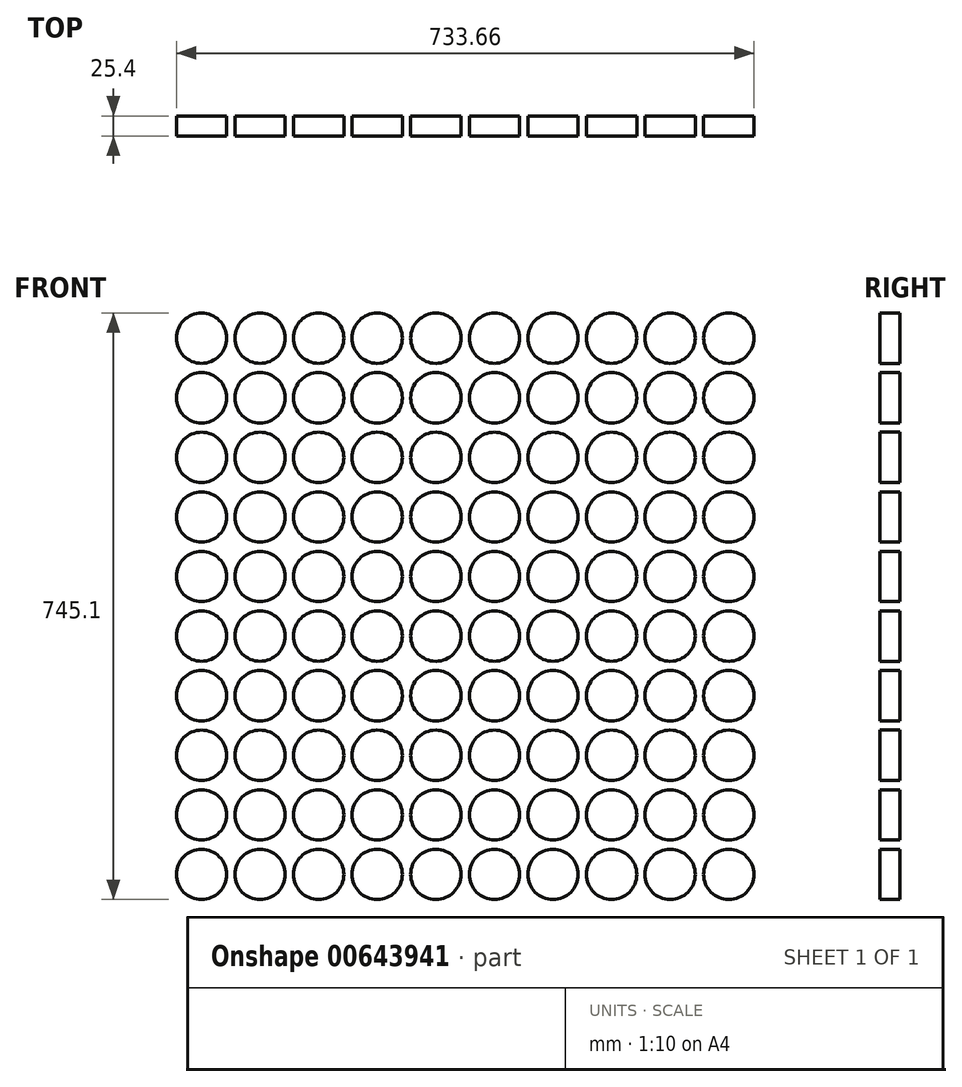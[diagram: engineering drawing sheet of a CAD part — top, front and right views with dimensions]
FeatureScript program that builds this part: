
annotation { "Feature Type Name" : "Feature", "Feature Type Description" : "" }
export const myFeature = defineFeature(function(context is Context, id is Id, definition is map)
    precondition{}
    {
        {
            var Q0;
            Q0=qCreatedBy(makeId("Front.planeOp"),FACE);
            var sketch = newSketch(context, id + "F0", { "sketchPlane" : qUnion([Q0])});
            skCircle(sketch, "E0", {"center": v(-124.64, -78.12) * mm, "radius": 31.93 * mm});
            skCircle(sketch, "E1.0.1.0", {"center": v(-124.64, -2.43) * mm, "radius": 31.93 * mm});
            skCircle(sketch, "E1.0.2.0", {"center": v(-124.64, 73.26) * mm, "radius": 31.93 * mm});
            skCircle(sketch, "E1.0.3.0", {"center": v(-124.64, 148.95) * mm, "radius": 31.93 * mm});
            skCircle(sketch, "E1.0.4.0", {"center": v(-124.64, 224.64) * mm, "radius": 31.93 * mm});
            skCircle(sketch, "E1.0.5.0", {"center": v(-124.64, 300.34) * mm, "radius": 31.93 * mm});
            skCircle(sketch, "E1.0.6.0", {"center": v(-124.64, 376.03) * mm, "radius": 31.93 * mm});
            skCircle(sketch, "E1.0.7.0", {"center": v(-124.64, 451.72) * mm, "radius": 31.93 * mm});
            skCircle(sketch, "E1.0.8.0", {"center": v(-124.64, 527.41) * mm, "radius": 31.93 * mm});
            skCircle(sketch, "E1.0.9.0", {"center": v(-124.64, 603.1) * mm, "radius": 31.93 * mm});
            skCircle(sketch, "E1.1.0.0", {"center": v(-50.22, -78.12) * mm, "radius": 31.93 * mm});
            skCircle(sketch, "E1.1.1.0", {"center": v(-50.22, -2.43) * mm, "radius": 31.93 * mm});
            skCircle(sketch, "E1.1.2.0", {"center": v(-50.22, 73.26) * mm, "radius": 31.93 * mm});
            skCircle(sketch, "E1.1.3.0", {"center": v(-50.22, 148.95) * mm, "radius": 31.93 * mm});
            skCircle(sketch, "E1.1.4.0", {"center": v(-50.22, 224.64) * mm, "radius": 31.93 * mm});
            skCircle(sketch, "E1.1.5.0", {"center": v(-50.22, 300.34) * mm, "radius": 31.93 * mm});
            skCircle(sketch, "E1.1.6.0", {"center": v(-50.22, 376.03) * mm, "radius": 31.93 * mm});
            skCircle(sketch, "E1.1.7.0", {"center": v(-50.22, 451.72) * mm, "radius": 31.93 * mm});
            skCircle(sketch, "E1.1.8.0", {"center": v(-50.22, 527.41) * mm, "radius": 31.93 * mm});
            skCircle(sketch, "E1.1.9.0", {"center": v(-50.22, 603.1) * mm, "radius": 31.93 * mm});
            skCircle(sketch, "E1.2.0.0", {"center": v(24.2, -78.12) * mm, "radius": 31.93 * mm});
            skCircle(sketch, "E1.2.1.0", {"center": v(24.2, -2.43) * mm, "radius": 31.93 * mm});
            skCircle(sketch, "E1.2.2.0", {"center": v(24.2, 73.26) * mm, "radius": 31.93 * mm});
            skCircle(sketch, "E1.2.3.0", {"center": v(24.2, 148.95) * mm, "radius": 31.93 * mm});
            skCircle(sketch, "E1.2.4.0", {"center": v(24.2, 224.64) * mm, "radius": 31.93 * mm});
            skCircle(sketch, "E1.2.5.0", {"center": v(24.2, 300.34) * mm, "radius": 31.93 * mm});
            skCircle(sketch, "E1.2.6.0", {"center": v(24.2, 376.03) * mm, "radius": 31.93 * mm});
            skCircle(sketch, "E1.2.7.0", {"center": v(24.2, 451.72) * mm, "radius": 31.93 * mm});
            skCircle(sketch, "E1.2.8.0", {"center": v(24.2, 527.41) * mm, "radius": 31.93 * mm});
            skCircle(sketch, "E1.2.9.0", {"center": v(24.2, 603.1) * mm, "radius": 31.93 * mm});
            skCircle(sketch, "E1.3.0.0", {"center": v(98.63, -78.12) * mm, "radius": 31.93 * mm});
            skCircle(sketch, "E1.3.1.0", {"center": v(98.63, -2.43) * mm, "radius": 31.93 * mm});
            skCircle(sketch, "E1.3.2.0", {"center": v(98.63, 73.26) * mm, "radius": 31.93 * mm});
            skCircle(sketch, "E1.3.3.0", {"center": v(98.63, 148.95) * mm, "radius": 31.93 * mm});
            skCircle(sketch, "E1.3.4.0", {"center": v(98.63, 224.64) * mm, "radius": 31.93 * mm});
            skCircle(sketch, "E1.3.5.0", {"center": v(98.63, 300.34) * mm, "radius": 31.93 * mm});
            skCircle(sketch, "E1.3.6.0", {"center": v(98.63, 376.03) * mm, "radius": 31.93 * mm});
            skCircle(sketch, "E1.3.7.0", {"center": v(98.63, 451.72) * mm, "radius": 31.93 * mm});
            skCircle(sketch, "E1.3.8.0", {"center": v(98.63, 527.41) * mm, "radius": 31.93 * mm});
            skCircle(sketch, "E1.3.9.0", {"center": v(98.63, 603.1) * mm, "radius": 31.93 * mm});
            skCircle(sketch, "E1.4.0.0", {"center": v(173.05, -78.12) * mm, "radius": 31.93 * mm});
            skCircle(sketch, "E1.4.1.0", {"center": v(173.05, -2.43) * mm, "radius": 31.93 * mm});
            skCircle(sketch, "E1.4.2.0", {"center": v(173.05, 73.26) * mm, "radius": 31.93 * mm});
            skCircle(sketch, "E1.4.3.0", {"center": v(173.05, 148.95) * mm, "radius": 31.93 * mm});
            skCircle(sketch, "E1.4.4.0", {"center": v(173.05, 224.64) * mm, "radius": 31.93 * mm});
            skCircle(sketch, "E1.4.5.0", {"center": v(173.05, 300.34) * mm, "radius": 31.93 * mm});
            skCircle(sketch, "E1.4.6.0", {"center": v(173.05, 376.03) * mm, "radius": 31.93 * mm});
            skCircle(sketch, "E1.4.7.0", {"center": v(173.05, 451.72) * mm, "radius": 31.93 * mm});
            skCircle(sketch, "E1.4.8.0", {"center": v(173.05, 527.41) * mm, "radius": 31.93 * mm});
            skCircle(sketch, "E1.4.9.0", {"center": v(173.05, 603.1) * mm, "radius": 31.93 * mm});
            skCircle(sketch, "E1.5.0.0", {"center": v(247.47, -78.12) * mm, "radius": 31.93 * mm});
            skCircle(sketch, "E1.5.1.0", {"center": v(247.47, -2.43) * mm, "radius": 31.93 * mm});
            skCircle(sketch, "E1.5.2.0", {"center": v(247.47, 73.26) * mm, "radius": 31.93 * mm});
            skCircle(sketch, "E1.5.3.0", {"center": v(247.47, 148.95) * mm, "radius": 31.93 * mm});
            skCircle(sketch, "E1.5.4.0", {"center": v(247.47, 224.64) * mm, "radius": 31.93 * mm});
            skCircle(sketch, "E1.5.5.0", {"center": v(247.47, 300.34) * mm, "radius": 31.93 * mm});
            skCircle(sketch, "E1.5.6.0", {"center": v(247.47, 376.03) * mm, "radius": 31.93 * mm});
            skCircle(sketch, "E1.5.7.0", {"center": v(247.47, 451.72) * mm, "radius": 31.93 * mm});
            skCircle(sketch, "E1.5.8.0", {"center": v(247.47, 527.41) * mm, "radius": 31.93 * mm});
            skCircle(sketch, "E1.5.9.0", {"center": v(247.47, 603.1) * mm, "radius": 31.93 * mm});
            skCircle(sketch, "E1.6.0.0", {"center": v(321.9, -78.12) * mm, "radius": 31.93 * mm});
            skCircle(sketch, "E1.6.1.0", {"center": v(321.9, -2.43) * mm, "radius": 31.93 * mm});
            skCircle(sketch, "E1.6.2.0", {"center": v(321.9, 73.26) * mm, "radius": 31.93 * mm});
            skCircle(sketch, "E1.6.3.0", {"center": v(321.9, 148.95) * mm, "radius": 31.93 * mm});
            skCircle(sketch, "E1.6.4.0", {"center": v(321.9, 224.64) * mm, "radius": 31.93 * mm});
            skCircle(sketch, "E1.6.5.0", {"center": v(321.9, 300.34) * mm, "radius": 31.93 * mm});
            skCircle(sketch, "E1.6.6.0", {"center": v(321.9, 376.03) * mm, "radius": 31.93 * mm});
            skCircle(sketch, "E1.6.7.0", {"center": v(321.9, 451.72) * mm, "radius": 31.93 * mm});
            skCircle(sketch, "E1.6.8.0", {"center": v(321.9, 527.41) * mm, "radius": 31.93 * mm});
            skCircle(sketch, "E1.6.9.0", {"center": v(321.9, 603.1) * mm, "radius": 31.93 * mm});
            skCircle(sketch, "E1.7.0.0", {"center": v(396.31, -78.12) * mm, "radius": 31.93 * mm});
            skCircle(sketch, "E1.7.1.0", {"center": v(396.31, -2.43) * mm, "radius": 31.93 * mm});
            skCircle(sketch, "E1.7.2.0", {"center": v(396.31, 73.26) * mm, "radius": 31.93 * mm});
            skCircle(sketch, "E1.7.3.0", {"center": v(396.31, 148.95) * mm, "radius": 31.93 * mm});
            skCircle(sketch, "E1.7.4.0", {"center": v(396.31, 224.64) * mm, "radius": 31.93 * mm});
            skCircle(sketch, "E1.7.5.0", {"center": v(396.31, 300.34) * mm, "radius": 31.93 * mm});
            skCircle(sketch, "E1.7.6.0", {"center": v(396.31, 376.03) * mm, "radius": 31.93 * mm});
            skCircle(sketch, "E1.7.7.0", {"center": v(396.31, 451.72) * mm, "radius": 31.93 * mm});
            skCircle(sketch, "E1.7.8.0", {"center": v(396.31, 527.41) * mm, "radius": 31.93 * mm});
            skCircle(sketch, "E1.7.9.0", {"center": v(396.31, 603.1) * mm, "radius": 31.93 * mm});
            skCircle(sketch, "E1.8.0.0", {"center": v(470.74, -78.12) * mm, "radius": 31.93 * mm});
            skCircle(sketch, "E1.8.1.0", {"center": v(470.74, -2.43) * mm, "radius": 31.93 * mm});
            skCircle(sketch, "E1.8.2.0", {"center": v(470.74, 73.26) * mm, "radius": 31.93 * mm});
            skCircle(sketch, "E1.8.3.0", {"center": v(470.74, 148.95) * mm, "radius": 31.93 * mm});
            skCircle(sketch, "E1.8.4.0", {"center": v(470.74, 224.64) * mm, "radius": 31.93 * mm});
            skCircle(sketch, "E1.8.5.0", {"center": v(470.74, 300.34) * mm, "radius": 31.93 * mm});
            skCircle(sketch, "E1.8.6.0", {"center": v(470.74, 376.03) * mm, "radius": 31.93 * mm});
            skCircle(sketch, "E1.8.7.0", {"center": v(470.74, 451.72) * mm, "radius": 31.93 * mm});
            skCircle(sketch, "E1.8.8.0", {"center": v(470.74, 527.41) * mm, "radius": 31.93 * mm});
            skCircle(sketch, "E1.8.9.0", {"center": v(470.74, 603.1) * mm, "radius": 31.93 * mm});
            skCircle(sketch, "E1.9.0.0", {"center": v(545.16, -78.12) * mm, "radius": 31.93 * mm});
            skCircle(sketch, "E1.9.1.0", {"center": v(545.16, -2.43) * mm, "radius": 31.93 * mm});
            skCircle(sketch, "E1.9.2.0", {"center": v(545.16, 73.26) * mm, "radius": 31.93 * mm});
            skCircle(sketch, "E1.9.3.0", {"center": v(545.16, 148.95) * mm, "radius": 31.93 * mm});
            skCircle(sketch, "E1.9.4.0", {"center": v(545.16, 224.64) * mm, "radius": 31.93 * mm});
            skCircle(sketch, "E1.9.5.0", {"center": v(545.16, 300.34) * mm, "radius": 31.93 * mm});
            skCircle(sketch, "E1.9.6.0", {"center": v(545.16, 376.03) * mm, "radius": 31.93 * mm});
            skCircle(sketch, "E1.9.7.0", {"center": v(545.16, 451.72) * mm, "radius": 31.93 * mm});
            skCircle(sketch, "E1.9.8.0", {"center": v(545.16, 527.41) * mm, "radius": 31.93 * mm});
            skCircle(sketch, "E1.9.9.0", {"center": v(545.16, 603.1) * mm, "radius": 31.93 * mm});
            skLineSegment(sketch, "E1.direction1", {"start": v(-124.64, -78.12) * mm, "end": v(-50.22, -78.12) * mm, "construction": true});
            skLineSegment(sketch, "E1.direction2", {"start": v(-124.64, -78.12) * mm, "end": v(-124.64, -2.43) * mm, "construction": true});
            skSolve(sketch);
        }
        {
            var Q0;
            Q0 = qSketchRegion(id + "F0", true);
            extrude(context, id + "F1", {"entities" : qUnion([Q0]), "depth" : 25.4 * mm, "offsetDistance" : 25.4 * mm});
        }
    });
